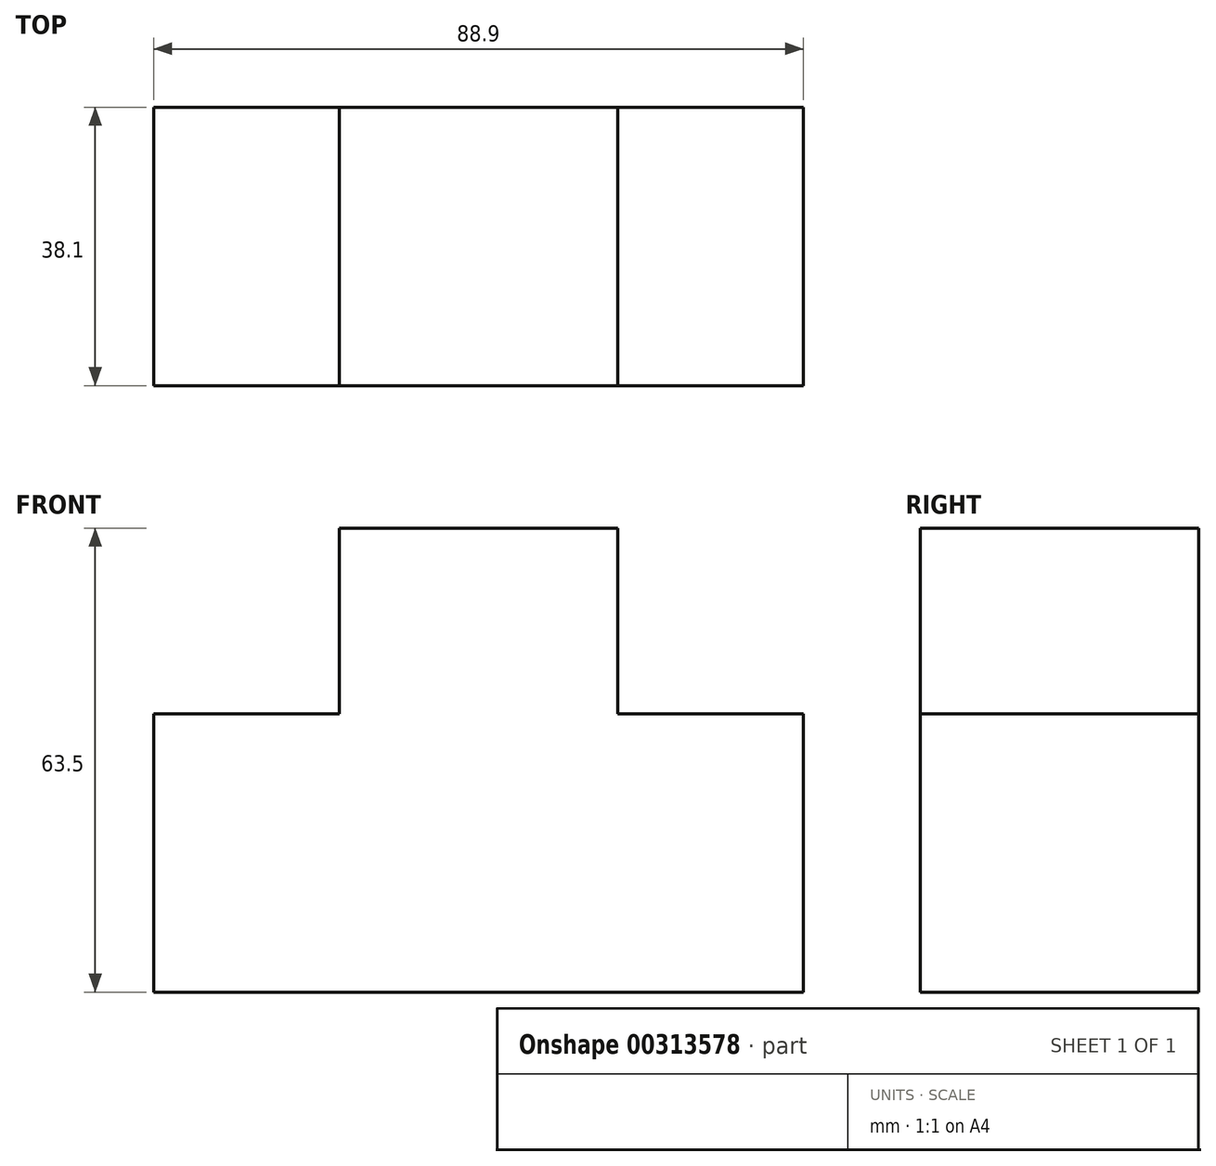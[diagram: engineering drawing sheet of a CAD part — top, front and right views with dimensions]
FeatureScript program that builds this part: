
annotation { "Feature Type Name" : "Feature", "Feature Type Description" : "" }
export const myFeature = defineFeature(function(context is Context, id is Id, definition is map)
    precondition{}
    {
        {
            var Q0;
            Q0=qCreatedBy(makeId("Front.planeOp"),FACE);
            var sketch = newSketch(context, id + "F0", { "sketchPlane" : qUnion([Q0])});
            skLineSegment(sketch, "E0", {"start": v(-48.9, -48.1) * mm, "end": v(40, -48.1) * mm});
            skLineSegment(sketch, "E1", {"start": v(40, -48.1) * mm, "end": v(40, -10) * mm});
            skLineSegment(sketch, "E2", {"start": v(40, -10) * mm, "end": v(14.6, -10) * mm});
            skLineSegment(sketch, "E3", {"start": v(14.6, -10) * mm, "end": v(14.6, 15.4) * mm});
            skLineSegment(sketch, "E4", {"start": v(14.6, 15.4) * mm, "end": v(-23.5, 15.4) * mm});
            skLineSegment(sketch, "E5", {"start": v(-23.5, 15.4) * mm, "end": v(-23.5, -10) * mm});
            skLineSegment(sketch, "E6", {"start": v(-48.9, -10) * mm, "end": v(-48.9, -48.1) * mm});
            skLineSegment(sketch, "E7", {"start": v(-48.9, -10) * mm, "end": v(-23.5, -10) * mm});
            skSolve(sketch);
        }
        {
            var Q0;
            Q0=makeQuery(id+"F0.imprint","IMPRINT",FACE,{"disambiguationData":[TD([[makeQuery(id+"F0.imprint","IMPRINT",EDGE,{"derivedFrom":sQuery(id+"F0.wireOp",EDGE,"E0")}),1.0]])]});
            extrude(context, id + "F1", {"entities" : qUnion([Q0]), "depth" : 38.1 * mm});
        }
    });
